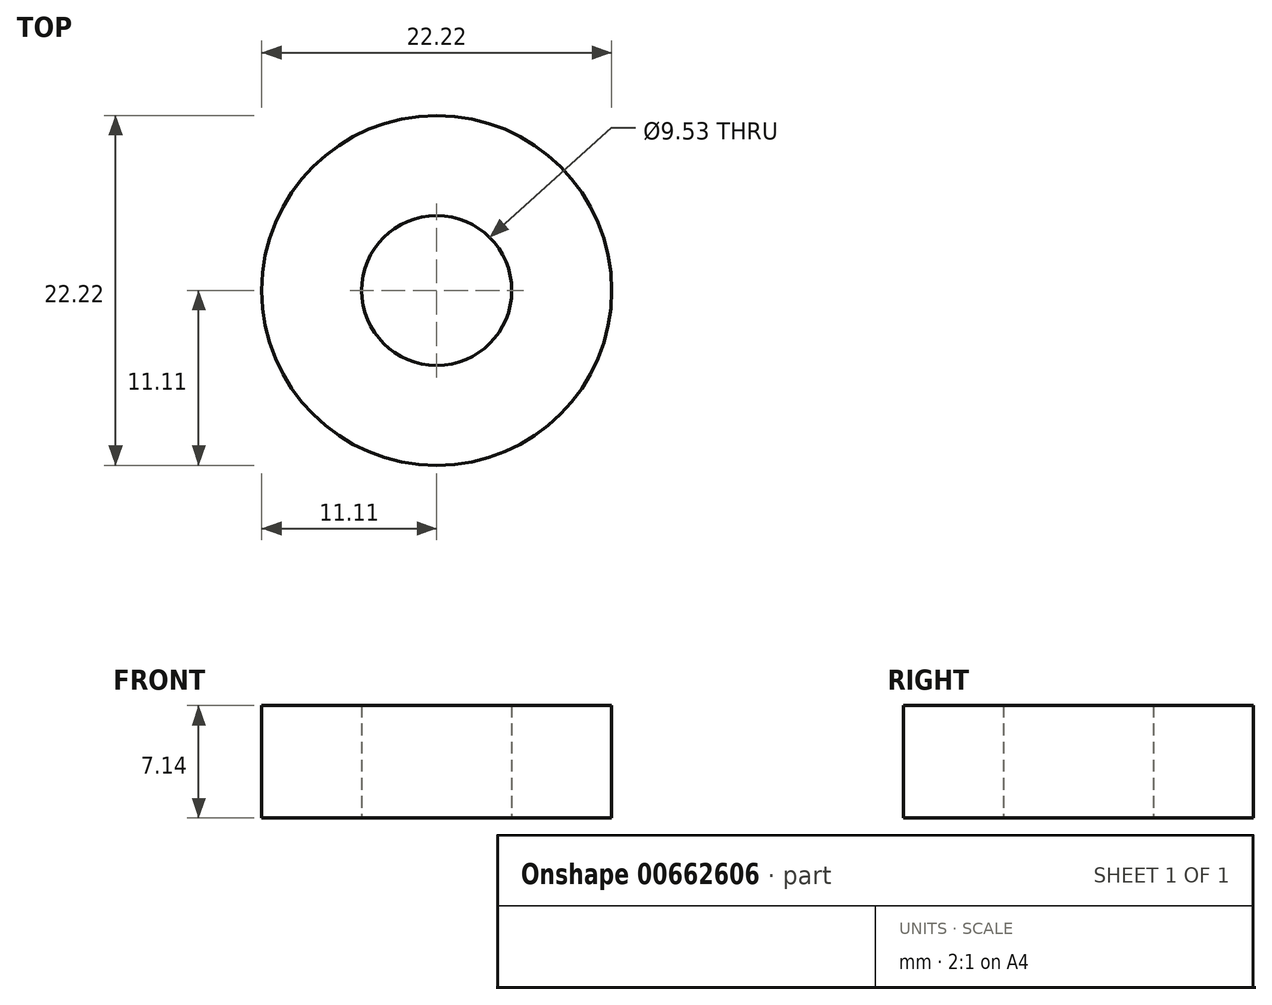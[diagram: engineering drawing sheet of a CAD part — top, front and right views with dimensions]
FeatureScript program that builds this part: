
annotation { "Feature Type Name" : "Feature", "Feature Type Description" : "" }
export const myFeature = defineFeature(function(context is Context, id is Id, definition is map)
    precondition{}
    {
        {
            var Q0;
            Q0=qCreatedBy(makeId("Top.planeOp"),FACE);
            var sketch = newSketch(context, id + "F0", { "sketchPlane" : qUnion([Q0])});
            skCircle(sketch, "E0", {"center": v(0, 0) * mm, "radius": 4.76 * mm});
            skCircle(sketch, "E1", {"center": v(0, 0) * mm, "radius": 11.11 * mm});
            skSolve(sketch);
        }
        {
            var Q0;
            Q0=makeQuery(id+"F0.imprint","IMPRINT",FACE,{"disambiguationData":[TD([[makeQuery(id+"F0.imprint","IMPRINT",EDGE,{"derivedFrom":sQuery(id+"F0.wireOp",EDGE,"E0")}),-1.0]])]});
            extrude(context, id + "F1", {"entities" : qUnion([Q0]), "depth" : 7.14 * mm, "offsetDistance" : 25.4 * mm});
        }
    });
